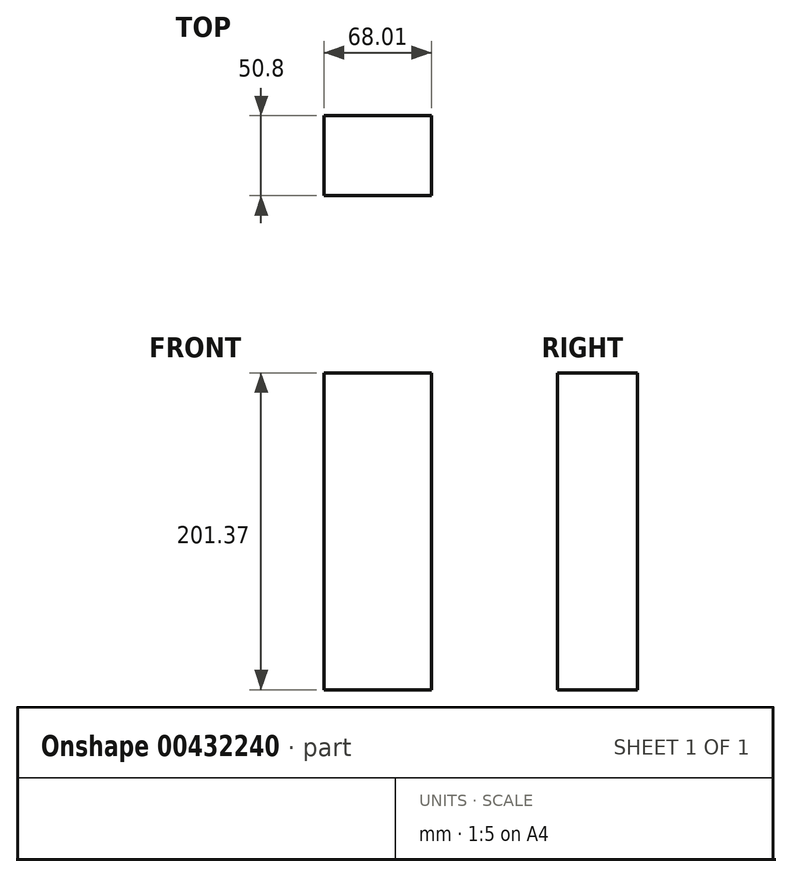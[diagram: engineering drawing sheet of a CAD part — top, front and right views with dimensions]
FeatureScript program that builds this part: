
annotation { "Feature Type Name" : "Feature", "Feature Type Description" : "" }
export const myFeature = defineFeature(function(context is Context, id is Id, definition is map)
    precondition{}
    {
        {
            var Q0;
            Q0=qCreatedBy(makeId("Front.planeOp"),FACE);
            var sketch = newSketch(context, id + "F0", { "sketchPlane" : qUnion([Q0])});
            skLineSegment(sketch, "E0.bottom", {"start": v(0, 0) * mm, "end": v(68, 0) * mm});
            skLineSegment(sketch, "E0.top", {"start": v(0, 201.37) * mm, "end": v(68, 201.37) * mm});
            skLineSegment(sketch, "E0.left", {"start": v(0, 0) * mm, "end": v(0, 201.37) * mm});
            skLineSegment(sketch, "E0.right", {"start": v(68, 0) * mm, "end": v(68, 201.37) * mm});
            skSolve(sketch);
        }
        {
            var Q0;
            Q0=makeQuery(id+"F0.imprint","IMPRINT",FACE,{"disambiguationData":[TD([[makeQuery(id+"F0.imprint","IMPRINT",EDGE,{"derivedFrom":sQuery(id+"F0.wireOp",EDGE,"E0.bottom")}),1.0]])]});
            extrude(context, id + "F1", {"entities" : qUnion([Q0]), "depth" : 50.8 * mm});
        }
    });
